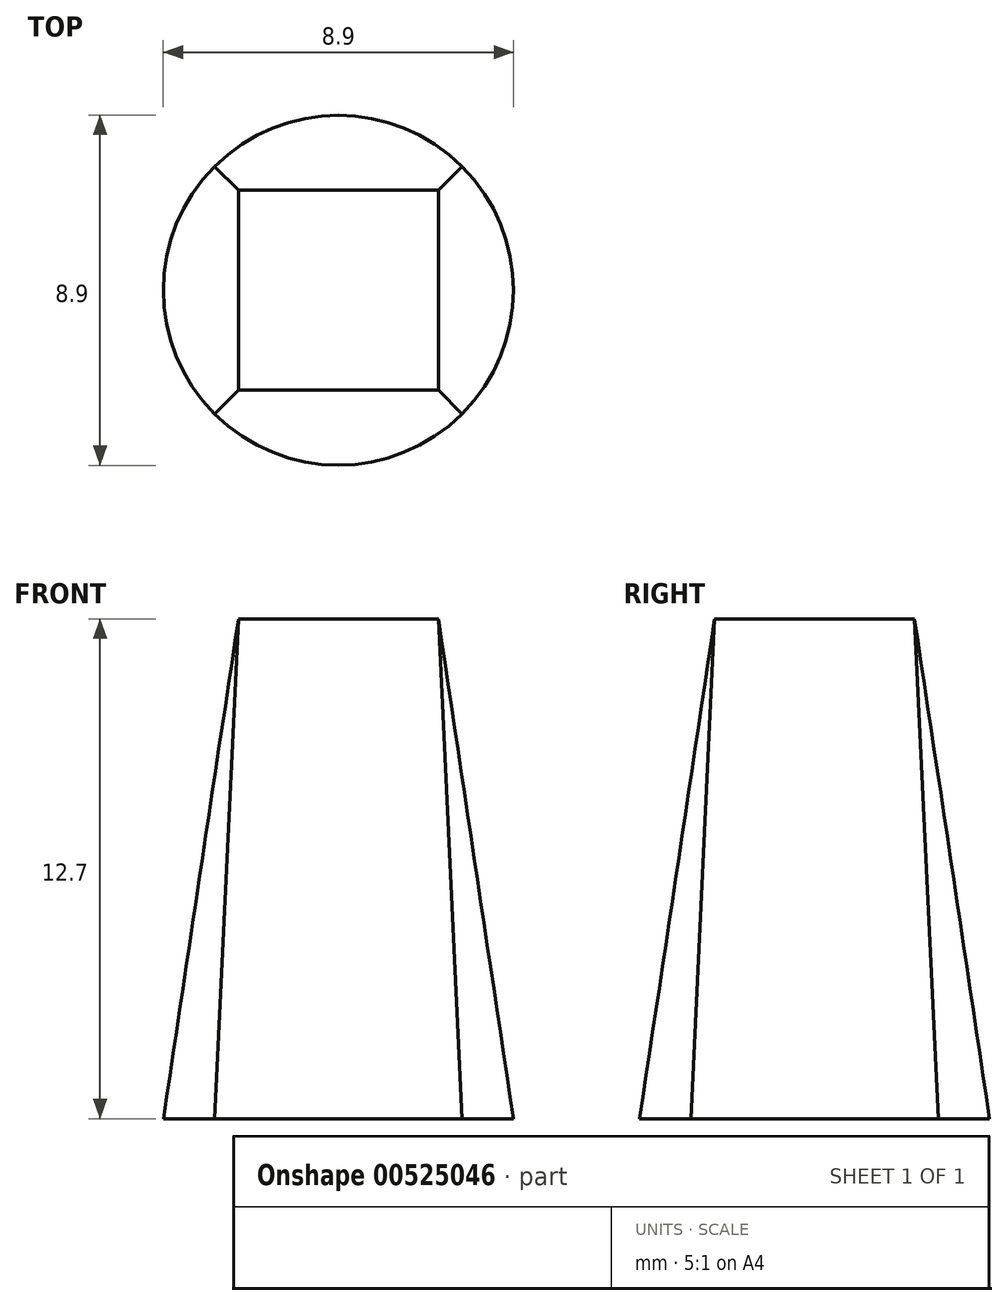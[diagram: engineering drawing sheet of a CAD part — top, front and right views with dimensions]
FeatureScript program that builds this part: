
annotation { "Feature Type Name" : "Feature", "Feature Type Description" : "" }
export const myFeature = defineFeature(function(context is Context, id is Id, definition is map)
    precondition{}
    {
        {
            var Q0;
            Q0=qCreatedBy(makeId("Top.planeOp"),FACE);
            var sketch = newSketch(context, id + "F0", { "sketchPlane" : qUnion([Q0])});
            skCircle(sketch, "E0", {"center": v(0, 0) * mm, "radius": 4.45 * mm});
            skSolve(sketch);
        }
        {
            var Q0;
            Q0=qCreatedBy(makeId("Top.planeOp"),FACE);
            cPlane(context, id + "F1", {"entities" : qUnion([Q0]), "cplaneType" : CPlaneType.OFFSET, "offset" : 12.7 * mm, "width" : 152.4 * mm, "height" : 152.4 * mm});
        }
        {
            var Q0;
            Q0=qCreatedBy(id+"F1.planeOp",FACE);
            var sketch = newSketch(context, id + "F2", { "sketchPlane" : qUnion([Q0])});
            skLineSegment(sketch, "E1.bottom", {"start": v(2.54, 2.54) * mm, "end": v(-2.54, 2.54) * mm});
            skLineSegment(sketch, "E1.top", {"start": v(2.54, -2.54) * mm, "end": v(-2.54, -2.54) * mm});
            skLineSegment(sketch, "E1.left", {"start": v(2.54, 2.54) * mm, "end": v(2.54, -2.54) * mm});
            skLineSegment(sketch, "E1.right", {"start": v(-2.54, 2.54) * mm, "end": v(-2.54, -2.54) * mm});
            skPoint(sketch, "E1.middle", {"position": v(0, 0) * mm});
            skSolve(sketch);
        }
        {
            var Q0;
            Q0=makeQuery(id+"F0.imprint","IMPRINT",FACE,{"disambiguationData":[TD([[makeQuery(id+"F0.imprint","IMPRINT",EDGE,{"derivedFrom":sQuery(id+"F0.wireOp",EDGE,"E0")}),1.0]])]});
            var Q1;
            Q1=makeQuery(id+"F2.imprint","IMPRINT",FACE,{"disambiguationData":[TD([[makeQuery(id+"F2.imprint","IMPRINT",EDGE,{"derivedFrom":sQuery(id+"F2.wireOp",EDGE,"E1.bottom")}),1.0]])]});
            loft(context, id + "F3", {"sheetProfilesArray" : [{ "sheetProfileEntities" : qUnion([Q0]) }, { "sheetProfileEntities" : qUnion([Q1]) }]});
        }
    });
